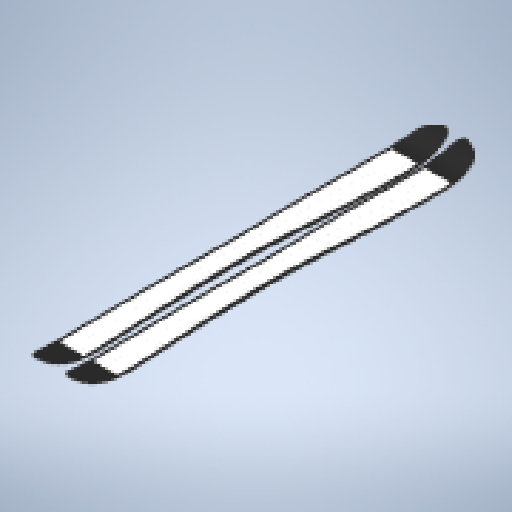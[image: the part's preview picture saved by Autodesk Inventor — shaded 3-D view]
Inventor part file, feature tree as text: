
AUTODESK INVENTOR PART (.ipt)
format: ipt  version: 2024 (Build 280153000, 153)  size: 1,767,424 bytes
history: native  units: in
note: dims shown in document units (in); Inventor stores cm internally (conversion verified against a paired STEP export)
features: other x17, mirror x17
ambient origin geometry x8: Origin, YZ Plane, XZ Plane, XY Plane, X Axis, Y Axis, Z Axis, Center Point
bodies: Solid1 (feature_tree), Solid2 (feature_tree), Solid3 (feature_tree), Solid4 (feature_tree), Solid5 (feature_tree), Solid6 (feature_tree), Solid7 (feature_tree), Solid8 (feature_tree), Solid9 (feature_tree), Solid10 (feature_tree), Solid11 (feature_tree), Solid12 (feature_tree), Solid13 (feature_tree), Solid14 (feature_tree), Solid15 (feature_tree), Solid16 (feature_tree), Solid17 (feature_tree), Solid18 (feature_tree), Solid19 (feature_tree), Solid20 (feature_tree), Solid21 (feature_tree), Solid22 (feature_tree), Solid23 (feature_tree), Solid24 (feature_tree), Solid25 (feature_tree), Solid26 (feature_tree), Solid27 (feature_tree), Solid28 (feature_tree), Solid29 (feature_tree), Solid30 (feature_tree), Solid31 (feature_tree), Solid32 (feature_tree), Solid33 (feature_tree), Solid34 (feature_tree)
feature tree (34):
  other  "Cut-Extrude3"
  other  "Cut-Extrude9"
  other  "Cut-Extrude10"
  other  "Cut-Extrude11"
  other  "Cut-Extrude15[1]"
  other  "Cut-Extrude15[2]"
  other  "Cut-Extrude15[3]"
  other  "Cut-Extrude16[1]"
  other  "Cut-Extrude16[2]"
  other  "Cut-Extrude16[3]"
  other  "Cut-Extrude16[4]"
  other  "Cut-Extrude16[5]"
  other  "Cut-Extrude16[6]"
  other  "Cut-Extrude17[1]"
  other  "Cut-Extrude17[2]"
  other  "Cut-Extrude18[1]"
  other  "Cut-Extrude18[2]"
  mirror  "Mirror2[1]"
  mirror  "Mirror2[2]"
  mirror  "Mirror2[3]"
  mirror  "Mirror2[4]"
  mirror  "Mirror2[5]"
  mirror  "Mirror2[6]"
  mirror  "Mirror2[7]"
  mirror  "Mirror2[8]"
  mirror  "Mirror2[9]"
  mirror  "Mirror2[10]"
  mirror  "Mirror2[11]"
  mirror  "Mirror2[12]"
  mirror  "Mirror2[13]"
  mirror  "Mirror2[14]"
  mirror  "Mirror2[15]"
  mirror  "Mirror2[16]"
  mirror  "Mirror2[17]"
